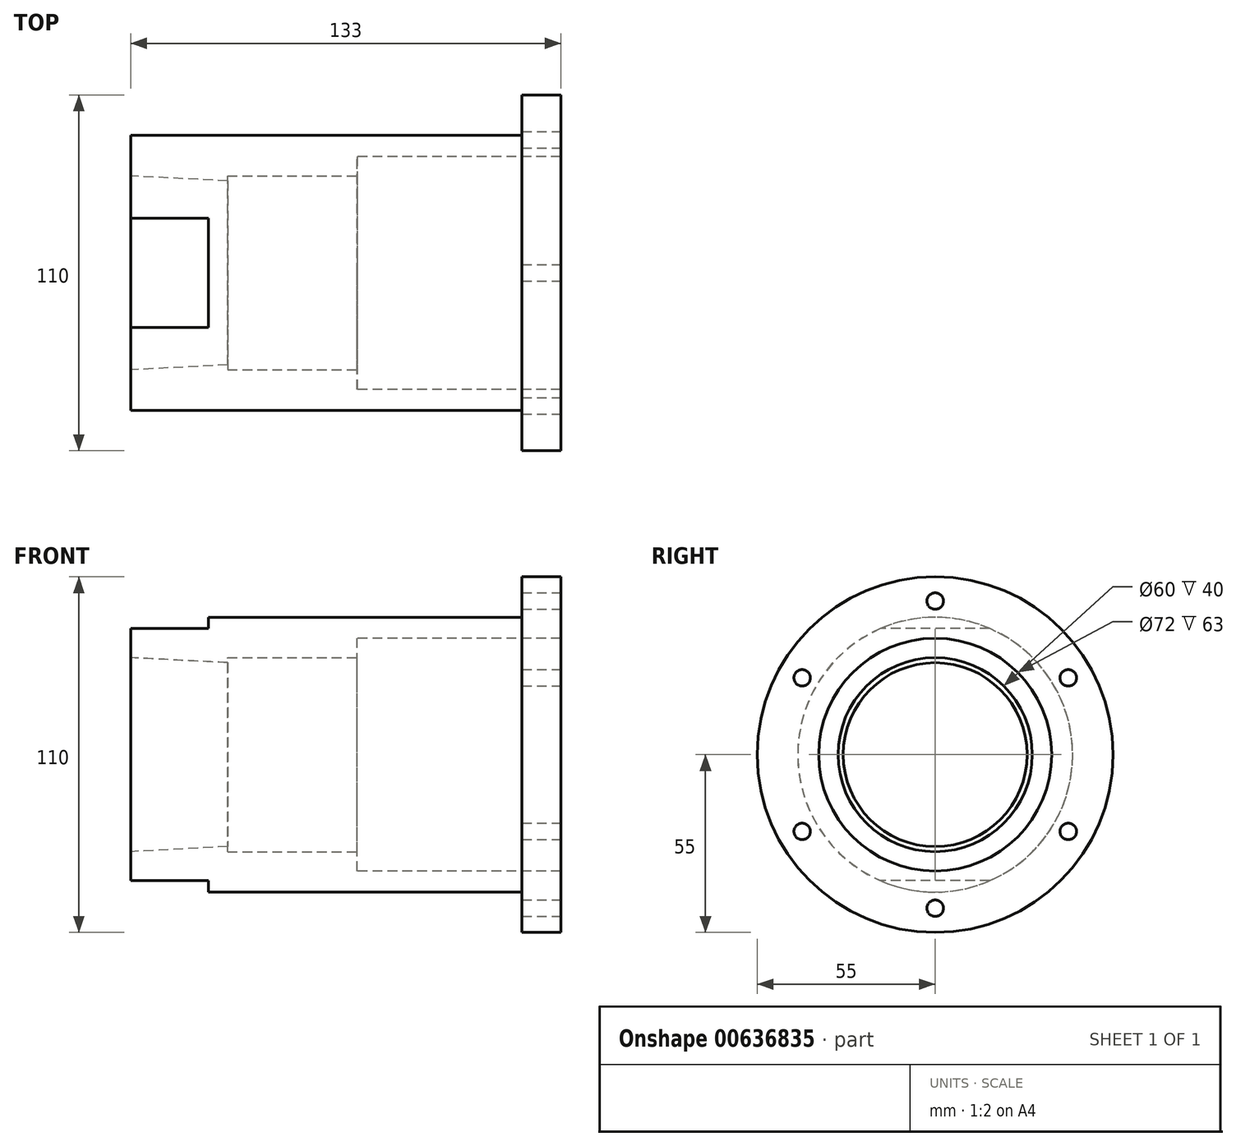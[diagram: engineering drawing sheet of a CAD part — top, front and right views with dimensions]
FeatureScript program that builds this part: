
annotation { "Feature Type Name" : "Feature", "Feature Type Description" : "" }
export const myFeature = defineFeature(function(context is Context, id is Id, definition is map)
    precondition{}
    {
        {
            var Q0;
            Q0=qCreatedBy(makeId("Right.planeOp"),FACE);
            var sketch = newSketch(context, id + "F0", { "sketchPlane" : qUnion([Q0])});
            skCircle(sketch, "E0", {"center": v(0, 0) * mm, "radius": 42.5 * mm});
            skSolve(sketch);
        }
        {
            var Q0;
            Q0 = qSketchRegion(id + "F0", true);
            extrude(context, id + "F1", {"entities" : qUnion([Q0]), "endBound" : BoundingType.SYMMETRIC, "depth" : 133 * mm, "offsetDistance" : 25 * mm});
        }
        {
            var Q0;
            Q0=makeQuery(id+"F1.opExtrude","CAP_FACE",FACE,{"disambiguationData":[OSD([sQuery(id+"F0.wireOp",EDGE,"E0")])],"isStart":false});
            var sketch = newSketch(context, id + "F2", { "sketchPlane" : qUnion([Q0])});
            skCircle(sketch, "E1", {"center": v(0, 0) * mm, "radius": 55 * mm});
            skSolve(sketch);
        }
        {
            var Q0;
            Q0 = qSketchRegion(id + "F2", true);
            extrude(context, id + "F3", {"entities" : qUnion([Q0]), "operationType" : NewBodyOperationType.ADD, "oppositeDirection" : true, "depth" : 12 * mm, "offsetDistance" : 25 * mm});
        }
        {
            var Q0;
            Q0=makeQuery(id+"F3.boolean.opBoolean","MERGE",FACE,{"derivedFrom":[makeQuery(id+"F1.opExtrude","CAP_FACE",FACE,{"disambiguationData":[OSD([sQuery(id+"F0.wireOp",EDGE,"E0")])],"isStart":false}),makeQuery(id+"F3.opExtrude","CAP_FACE",FACE,{"disambiguationData":[OSD([sQuery(id+"F2.wireOp",EDGE,"E1")])],"isStart":true})]});
            var sketch = newSketch(context, id + "F4", { "sketchPlane" : qUnion([Q0])});
            skCircle(sketch, "E2", {"center": v(0, 0) * mm, "radius": 47.5 * mm, "construction": true});
            skLineSegment(sketch, "E3", {"start": v(0, 0) * mm, "end": v(0, 60.52) * mm});
            skPoint(sketch, "E4", {"position": v(0, 47.5) * mm});
            skPoint(sketch, "E5.1.0", {"position": v(-41.14, 23.75) * mm});
            skPoint(sketch, "E5.2.0", {"position": v(-41.14, -23.75) * mm});
            skPoint(sketch, "E5.3.0", {"position": v(0, -47.5) * mm});
            skPoint(sketch, "E5.4.0", {"position": v(41.14, -23.75) * mm});
            skPoint(sketch, "E5.5.0", {"position": v(41.14, 23.75) * mm});
            skSolve(sketch);
        }
        {
            var Q0;
            Q0=sQuery(id+"F4.wireOp",VERTEX,"E4");
            var Q1;
            Q1=sQuery(id+"F4.wireOp",VERTEX,"E5.1.0");
            var Q2;
            Q2=sQuery(id+"F4.wireOp",VERTEX,"E5.2.0");
            var Q3;
            Q3=sQuery(id+"F4.wireOp",VERTEX,"E5.3.0");
            var Q4;
            Q4=sQuery(id+"F4.wireOp",VERTEX,"E5.4.0");
            var Q5;
            Q5=sQuery(id+"F4.wireOp",VERTEX,"E5.5.0");
            var Q6;
            Q6=makeQuery(id+"F1.opExtrude","SWEPT_BODY",BODY,{"disambiguationData":[OSD([sQuery(id+"F0.wireOp",EDGE,"E0")])]});
            hole(context, id + "F5", {"style" : HoleStyle.SIMPLE, "endStyle" : HoleEndStyle.THROUGH, "standardTappedOrClearance" : lookupTablePath({ "standard" : "ANSI", "engagement" : "75%", "pitch" : "20 tpi", "size" : "1/4", "type" : "Tapped" }), "standardBlindInLast" : lookupTablePath({ "standard" : "ANSI", "engagement" : "75%", "pitch" : "20 tpi", "size" : "1/4", "type" : "Tapped" }), "holeDiameter" : 5.1 * mm, "majorDiameter" : 6.35 * mm, "showTappedDepth" : true, "isTappedThrough" : true, "tappedDepth" : 12 * mm, "tapClearance" : 3, "startFromSketch" : true, "locations" : qUnion([Q0, Q1, Q2, Q3, Q4, Q5]), "scope" : qUnion([Q6])});
        }
        {
            var Q0;
            Q0=makeQuery(id+"F1.opExtrude","CAP_FACE",FACE,{"disambiguationData":[OSD([sQuery(id+"F0.wireOp",EDGE,"E0")])],"isStart":true});
            var sketch = newSketch(context, id + "F6", { "sketchPlane" : qUnion([Q0])});
            skCircle(sketch, "E6", {"center": v(0, 0) * mm, "radius": 30 * mm});
            skSolve(sketch);
        }
        {
            var Q0;
            Q0 = qSketchRegion(id + "F6", true);
            extrude(context, id + "F7", {"entities" : qUnion([Q0]), "operationType" : NewBodyOperationType.REMOVE, "oppositeDirection" : true, "depth" : 30 * mm, "offsetDistance" : 25 * mm, "hasDraft" : true, "draftAngle" : 3 * degree, "draftPullDirection" : true});
        }
        {
            var Q0;
            Q0=makeQuery(id+"F3.boolean.opBoolean","MERGE",FACE,{"derivedFrom":[makeQuery(id+"F1.opExtrude","CAP_FACE",FACE,{"disambiguationData":[OSD([sQuery(id+"F0.wireOp",EDGE,"E0")])],"isStart":false}),makeQuery(id+"F3.opExtrude","CAP_FACE",FACE,{"disambiguationData":[OSD([sQuery(id+"F2.wireOp",EDGE,"E1")])],"isStart":true})]});
            var sketch = newSketch(context, id + "F8", { "sketchPlane" : qUnion([Q0])});
            skCircle(sketch, "E7", {"center": v(0, 0) * mm, "radius": 30 * mm});
            skSolve(sketch);
        }
        {
            var Q0;
            Q0 = qSketchRegion(id + "F8", true);
            var Q1;
            Q1=makeQuery(id+"F7.boolean.opBoolean","COPY",FACE,{"derivedFrom":makeQuery(id+"F7.opExtrude","CAP_FACE",FACE,{"disambiguationData":[OSD([sQuery(id+"F6.wireOp",EDGE,"E6")])],"isStart":false})});
            extrude(context, id + "F9", {"entities" : qUnion([Q0]), "operationType" : NewBodyOperationType.REMOVE, "endBound" : BoundingType.UP_TO_SURFACE, "oppositeDirection" : true, "depth" : 25 * mm, "endBoundEntityFace" : qUnion([Q1]), "offsetDistance" : 25 * mm});
        }
        {
            var Q0;
            Q0=makeQuery(id+"F9.boolean.opBoolean","COPY",FACE,{"derivedFrom":makeQuery(id+"F9.opExtrude","CAP_FACE",FACE,{"disambiguationData":[OSD([sQuery(id+"F8.wireOp",EDGE,"E7")])],"isStart":false})});
            cPlane(context, id + "F10", {"entities" : qUnion([Q0]), "cplaneType" : CPlaneType.OFFSET, "offset" : 40 * mm, "width" : 150 * mm, "height" : 150 * mm});
        }
        {
            var Q0;
            Q0=qCreatedBy(id+"F10.planeOp",FACE);
            var sketch = newSketch(context, id + "F11", { "sketchPlane" : qUnion([Q0])});
            skCircle(sketch, "E8", {"center": v(0, 0) * mm, "radius": 36 * mm});
            skSolve(sketch);
        }
        {
            var Q0;
            Q0 = qSketchRegion(id + "F11", true);
            var Q1;
            Q1=makeQuery(id+"F3.boolean.opBoolean","MERGE",FACE,{"derivedFrom":[makeQuery(id+"F1.opExtrude","CAP_FACE",FACE,{"disambiguationData":[OSD([sQuery(id+"F0.wireOp",EDGE,"E0")])],"isStart":false}),makeQuery(id+"F3.opExtrude","CAP_FACE",FACE,{"disambiguationData":[OSD([sQuery(id+"F2.wireOp",EDGE,"E1")])],"isStart":true})]});
            extrude(context, id + "F12", {"entities" : qUnion([Q0]), "operationType" : NewBodyOperationType.REMOVE, "endBound" : BoundingType.UP_TO_SURFACE, "depth" : 25 * mm, "endBoundEntityFace" : qUnion([Q1]), "offsetDistance" : 25 * mm});
        }
        {
            var Q0;
            Q0=makeQuery(id+"F1.opExtrude","CAP_FACE",FACE,{"disambiguationData":[OSD([sQuery(id+"F0.wireOp",EDGE,"E0")])],"isStart":true});
            var sketch = newSketch(context, id + "F13", { "sketchPlane" : qUnion([Q0])});
            skLineSegment(sketch, "E9", {"start": v(-101.94, 0) * mm, "end": v(98.23, 0) * mm, "construction": true});
            skLineSegment(sketch, "E10", {"start": v(0, 0) * mm, "end": v(0, 39) * mm, "construction": true});
            skLineSegment(sketch, "E11", {"start": v(0, 39) * mm, "end": v(-52.95, 39) * mm, "construction": true});
            skLineSegment(sketch, "E12.bottom", {"start": v(-52.95, 39) * mm, "end": v(52.49, 39) * mm});
            skLineSegment(sketch, "E12.top", {"start": v(-52.95, 57.31) * mm, "end": v(52.49, 57.31) * mm});
            skLineSegment(sketch, "E12.left", {"start": v(-52.95, 39) * mm, "end": v(-52.95, 57.31) * mm});
            skLineSegment(sketch, "E12.right", {"start": v(52.49, 39) * mm, "end": v(52.49, 57.31) * mm});
            skLineSegment(sketch, "E13.MirrorCS", {"start": v(-52.95, -39) * mm, "end": v(52.49, -39) * mm});
            skLineSegment(sketch, "E14.MirrorCS", {"start": v(0, -39) * mm, "end": v(-52.95, -39) * mm, "construction": true});
            skLineSegment(sketch, "E15.MirrorCS", {"start": v(-52.95, -57.31) * mm, "end": v(52.49, -57.31) * mm});
            skLineSegment(sketch, "E16.MirrorCS", {"start": v(-52.95, -39) * mm, "end": v(-52.95, -57.31) * mm});
            skLineSegment(sketch, "E17.MirrorCS", {"start": v(52.49, -39) * mm, "end": v(52.49, -57.31) * mm});
            skSolve(sketch);
        }
        {
            var Q0;
            Q0 = qSketchRegion(id + "F13", true);
            extrude(context, id + "F14", {"entities" : qUnion([Q0]), "operationType" : NewBodyOperationType.REMOVE, "oppositeDirection" : true, "depth" : 24 * mm, "offsetDistance" : 25 * mm});
        }
    });
